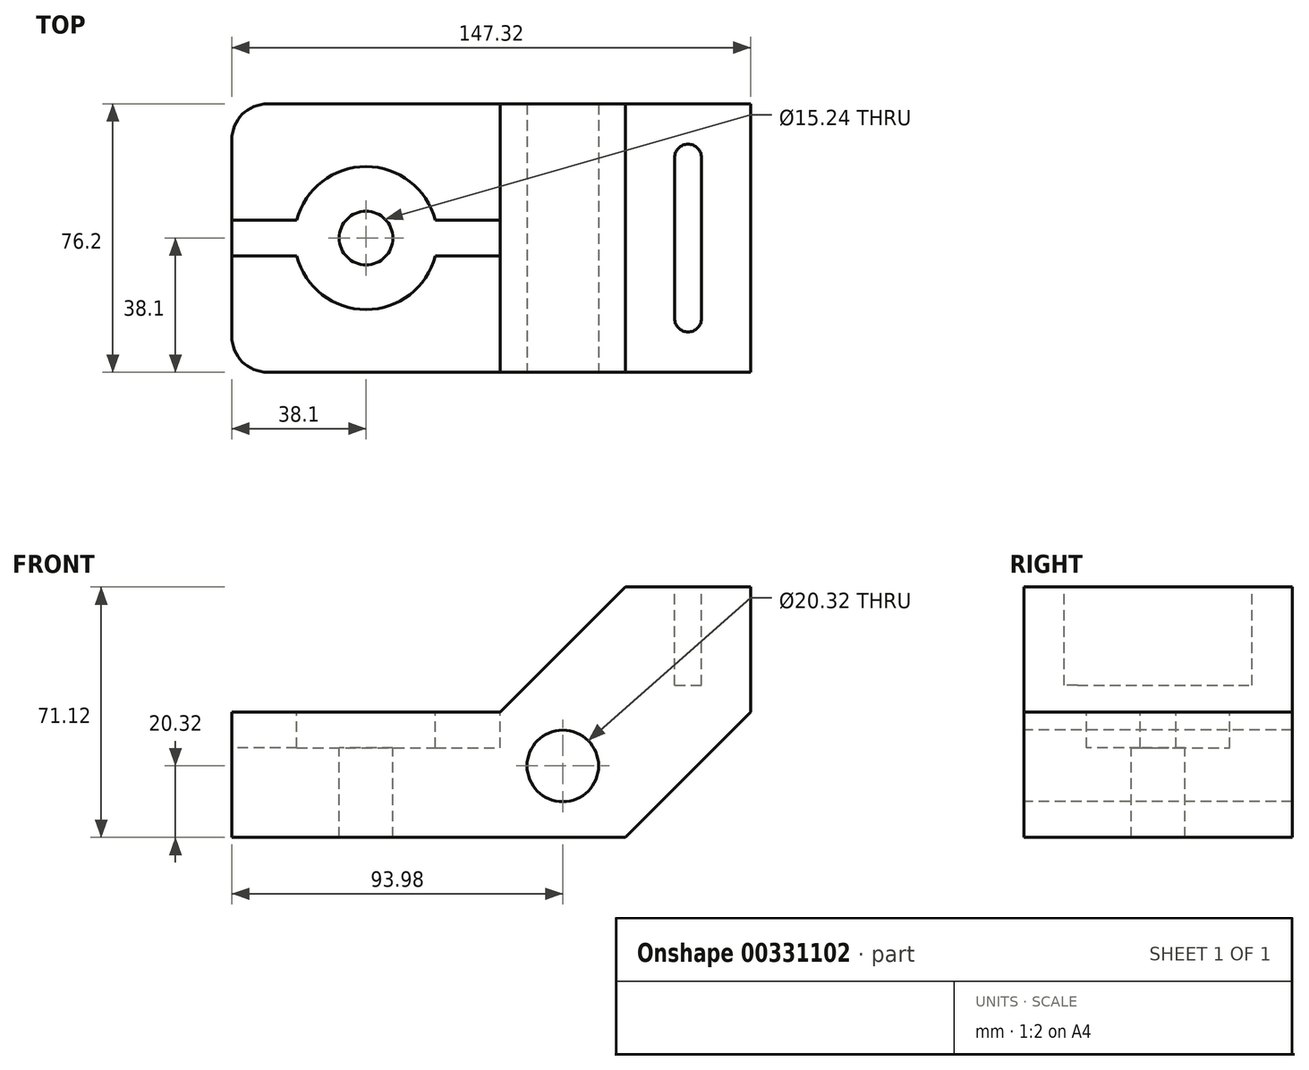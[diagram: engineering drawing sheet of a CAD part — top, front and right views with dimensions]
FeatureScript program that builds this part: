
annotation { "Feature Type Name" : "Feature", "Feature Type Description" : "" }
export const myFeature = defineFeature(function(context is Context, id is Id, definition is map)
    precondition{}
    {
        {
            var Q0;
            Q0=qCreatedBy(makeId("Front.planeOp"),FACE);
            var sketch = newSketch(context, id + "F0", { "sketchPlane" : qUnion([Q0])});
            skLineSegment(sketch, "E0", {"start": v(0, 0) * mm, "end": v(111.76, 0) * mm});
            skLineSegment(sketch, "E1", {"start": v(111.76, 0) * mm, "end": v(147.32, 35.56) * mm});
            skLineSegment(sketch, "E2", {"start": v(147.32, 35.56) * mm, "end": v(147.32, 71.12) * mm});
            skLineSegment(sketch, "E3", {"start": v(147.32, 71.12) * mm, "end": v(111.76, 71.12) * mm});
            skLineSegment(sketch, "E4", {"start": v(0, 0) * mm, "end": v(0, 35.56) * mm});
            skLineSegment(sketch, "E5", {"start": v(0, 35.56) * mm, "end": v(76.2, 35.56) * mm});
            skLineSegment(sketch, "E6", {"start": v(76.2, 35.56) * mm, "end": v(111.76, 71.12) * mm});
            skSolve(sketch);
        }
        {
            var Q0;
            Q0 = qSketchRegion(id + "F0", true);
            extrude(context, id + "F1", {"entities" : qUnion([Q0]), "depth" : 76.2 * mm});
        }
        {
            var Q0;
            Q0=makeQuery(id+"F1.opExtrude","CAP_FACE",FACE,{"disambiguationData":[OSD([sQuery(id+"F0.wireOp",EDGE,"E0"),sQuery(id+"F0.wireOp",EDGE,"E1"),sQuery(id+"F0.wireOp",EDGE,"E2"),sQuery(id+"F0.wireOp",EDGE,"E3"),sQuery(id+"F0.wireOp",EDGE,"E4"),sQuery(id+"F0.wireOp",EDGE,"E5"),sQuery(id+"F0.wireOp",EDGE,"E6")])],"isStart":false});
            var sketch = newSketch(context, id + "F2", { "sketchPlane" : qUnion([Q0])});
            skLineSegment(sketch, "E7", {"start": v(147.32, 35.56) * mm, "end": v(93.98, 35.56) * mm});
            skLineSegment(sketch, "E8", {"start": v(93.98, 35.56) * mm, "end": v(93.98, 0) * mm});
            skLineSegment(sketch, "E9", {"start": v(93.98, 0) * mm, "end": v(93.98, 20.32) * mm});
            skCircle(sketch, "E10", {"center": v(93.98, 20.32) * mm, "radius": 10.16 * mm});
            skSolve(sketch);
        }
        {
            var Q0;
            Q0 = qSketchRegion(id + "F2", true);
            extrude(context, id + "F3", {"entities" : qUnion([Q0]), "operationType" : NewBodyOperationType.REMOVE, "oppositeDirection" : true, "depth" : 177.8 * mm});
        }
        {
            var Q0;
            Q0=makeQuery(id+"F1.opExtrude","SWEPT_FACE",FACE,{"disambiguationData":[OSD([sQuery(id+"F0.wireOp",EDGE,"E3")])]});
            var sketch = newSketch(context, id + "F4", { "sketchPlane" : qUnion([Q0])});
            skLineSegment(sketch, "E11", {"start": v(147.32, 0) * mm, "end": v(129.54, 0) * mm});
            skLineSegment(sketch, "E12", {"start": v(129.54, 0) * mm, "end": v(129.54, -76.2) * mm});
            skLineSegment(sketch, "E13", {"start": v(129.54, -76.2) * mm, "end": v(129.54, -60.96) * mm});
            skLineSegment(sketch, "E14", {"start": v(129.54, -60.96) * mm, "end": v(129.54, 0) * mm});
            skLineSegment(sketch, "E15", {"start": v(129.54, 0) * mm, "end": v(129.54, -15.24) * mm});
            skCircle(sketch, "E16", {"center": v(129.54, -15.24) * mm, "radius": 3.81 * mm});
            skCircle(sketch, "E17", {"center": v(129.54, -60.96) * mm, "radius": 3.81 * mm});
            skLineSegment(sketch, "E18", {"start": v(129.54, -60.96) * mm, "end": v(125.73, -60.96) * mm});
            skLineSegment(sketch, "E19", {"start": v(125.73, -60.96) * mm, "end": v(133.35, -60.96) * mm});
            skLineSegment(sketch, "E20", {"start": v(133.35, -60.96) * mm, "end": v(133.35, -15.24) * mm});
            skLineSegment(sketch, "E21", {"start": v(133.35, -15.24) * mm, "end": v(125.73, -15.24) * mm});
            skLineSegment(sketch, "E22", {"start": v(125.73, -15.24) * mm, "end": v(125.73, -60.96) * mm});
            skSolve(sketch);
        }
        {
            var Q0;
            Q0 = qSketchRegion(id + "F4", true);
            extrude(context, id + "F5", {"entities" : qUnion([Q0]), "operationType" : NewBodyOperationType.REMOVE, "oppositeDirection" : true, "depth" : 27.94 * mm});
        }
        {
            var Q0;
            Q0=makeQuery(id+"F1.opExtrude","SWEPT_FACE",FACE,{"disambiguationData":[OSD([sQuery(id+"F0.wireOp",EDGE,"E5")])]});
            var sketch = newSketch(context, id + "F6", { "sketchPlane" : qUnion([Q0])});
            skLineSegment(sketch, "E23", {"start": v(0, 0) * mm, "end": v(0, -38.1) * mm});
            skLineSegment(sketch, "E24", {"start": v(0, -38.1) * mm, "end": v(0, -33.02) * mm});
            skLineSegment(sketch, "E25", {"start": v(0, -33.02) * mm, "end": v(0, -38.1) * mm});
            skLineSegment(sketch, "E26", {"start": v(0, -38.1) * mm, "end": v(0, -43.18) * mm});
            skLineSegment(sketch, "E27", {"start": v(0, -43.18) * mm, "end": v(76.2, -43.18) * mm});
            skLineSegment(sketch, "E28", {"start": v(76.2, -43.18) * mm, "end": v(76.2, -33.02) * mm});
            skPoint(sketch, "E28.endSnap0", {"position": v(76.2, -38.1) * mm});
            skLineSegment(sketch, "E29", {"start": v(76.2, -33.02) * mm, "end": v(0, -33.02) * mm});
            skLineSegment(sketch, "E30", {"start": v(0, -38.1) * mm, "end": v(76.2, -38.1) * mm});
            skCircle(sketch, "E31", {"center": v(38.1, -38.1) * mm, "radius": 20.32 * mm});
            skSolve(sketch);
        }
        {
            var Q0;
            Q0 = qSketchRegion(id + "F6", true);
            extrude(context, id + "F7", {"entities" : qUnion([Q0]), "operationType" : NewBodyOperationType.REMOVE, "oppositeDirection" : true, "depth" : 10.16 * mm});
        }
        {
            var Q0;
            Q0=makeQuery(id+"F7.boolean.opBoolean","COPY",FACE,{"derivedFrom":makeQuery(id+"F7.opExtrude","CAP_FACE",FACE,{"disambiguationData":[OSD([sQuery(id+"F6.wireOp",EDGE,"E25"),sQuery(id+"F6.wireOp",EDGE,"E26"),sQuery(id+"F6.wireOp",EDGE,"E27"),sQuery(id+"F6.wireOp",EDGE,"E28"),sQuery(id+"F6.wireOp",EDGE,"E29"),sQuery(id+"F6.wireOp",EDGE,"E31")])],"isStart":false})});
            var sketch = newSketch(context, id + "F8", { "sketchPlane" : qUnion([Q0])});
            skCircle(sketch, "E32", {"center": v(38.1, -38.1) * mm, "radius": 7.62 * mm});
            skSolve(sketch);
        }
        {
            var Q0;
            Q0 = qSketchRegion(id + "F8", true);
            extrude(context, id + "F9", {"entities" : qUnion([Q0]), "operationType" : NewBodyOperationType.REMOVE, "oppositeDirection" : true, "depth" : 152.4 * mm});
        }
        {
            var Q0;
            Q0=makeQuery(id+"F1.opExtrude","CAP_EDGE",EDGE,{"disambiguationData":[OSD([sQuery(id+"F0.wireOp",EDGE,"E4")])],"isStart":false});
            var Q1;
            Q1=makeQuery(id+"F1.opExtrude","CAP_EDGE",EDGE,{"disambiguationData":[OSD([sQuery(id+"F0.wireOp",EDGE,"E4")])],"isStart":true});
            fillet(context, id + "F10", {"entities" : qUnion([Q0, Q1]), "radius" : 10.16 * mm, "tangentPropagation" : true, "allowEdgeOverflow" : false});
        }
    });
